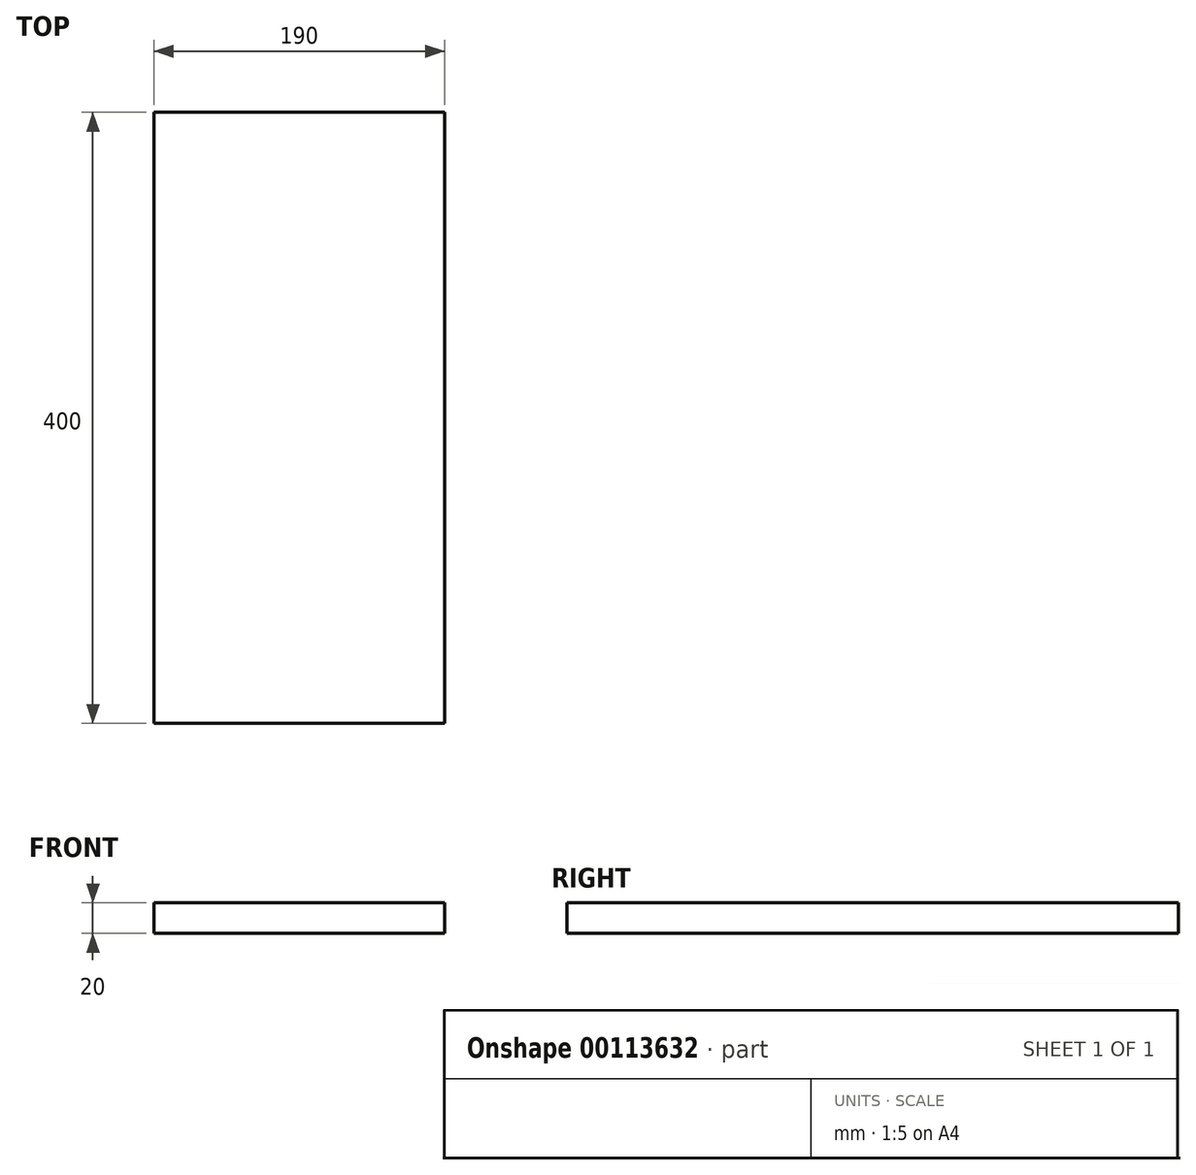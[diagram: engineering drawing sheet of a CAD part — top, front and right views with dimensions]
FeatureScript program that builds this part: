
annotation { "Feature Type Name" : "Feature", "Feature Type Description" : "" }
export const myFeature = defineFeature(function(context is Context, id is Id, definition is map)
    precondition{}
    {
        {
            var Q0;
            Q0=qCreatedBy(makeId("Front.planeOp"),FACE);
            var sketch = newSketch(context, id + "F0", { "sketchPlane" : qUnion([Q0])});
            skLineSegment(sketch, "E0.bottom", {"start": v(0, 0) * mm, "end": v(190, 0) * mm});
            skLineSegment(sketch, "E0.top", {"start": v(0, 20) * mm, "end": v(190, 20) * mm});
            skLineSegment(sketch, "E0.left", {"start": v(0, 0) * mm, "end": v(0, 20) * mm});
            skLineSegment(sketch, "E0.right", {"start": v(190, 0) * mm, "end": v(190, 20) * mm});
            skSolve(sketch);
        }
        {
            var Q0;
            Q0=makeQuery(id+"F0.imprint","IMPRINT",FACE,{"disambiguationData":[TD([[makeQuery(id+"F0.imprint","IMPRINT",EDGE,{"derivedFrom":sQuery(id+"F0.wireOp",EDGE,"E0.bottom")}),1.0]])]});
            extrude(context, id + "F1", {"entities" : qUnion([Q0]), "depth" : 400 * mm});
        }
    });
